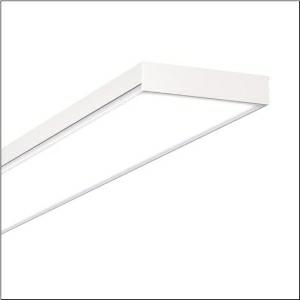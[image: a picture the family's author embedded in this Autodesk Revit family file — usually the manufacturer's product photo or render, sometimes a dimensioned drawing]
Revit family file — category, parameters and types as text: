
# Revit family: apollon_r__31_51mp26wm2441w_e1c8
name_source: partatom
category: Lighting Fixtures
units: mm (PartAtom-declared; Revit-internal decimal feet)

## family parameters
Cut with Voids When Loaded = No
Host = Face
Light Source = No
Part Type = Normal
Room Calculation Point = No
Round Connector Dimension = Use Diameter
Shared = No

## types (1)
- Apollon® 31 (1 x LED, 4600 lm, 33 W, 4000K)
    Apparent Load = 33 VA
    CIE Flux Codes = 61 87 97 97 100
    Color Rendering = 80
    Color Temperature = 4000K
    Default Elevation = 1800 mm
    Description = Apollon® 31, office luminaire, primary optical cover: micro prismatic cover, of PMMA, light emission: direct distribution, primary light characteristic: symmetric, installation type: surface-mounted, LED, rated luminous flux: 4.600lm, luminous efficacy: 139lm/W, light colour: 840, colour temperature: 4000K, control gear: ECG Multilumen, with terminal, 3-pole, mains connection: 220..240V, AC, 50/60Hz, rated input power: 33W, housing, of sheet steel, coil coated, traffic white (RAL 9016), length: 1.545mm, width: 200mm, height: 44mm, protection rating (complete): IP20, insulation class (complete): insulation class II (safety insulation), certification: CE, impact resistance: IK02, permissible operating ambient temperature: -20..+40°C, packaging unit: 1 piece
    Height = 44 mm
    Lamp = 1 x LED
    Lamp Light Flux = 4600 lm
    Lamp Power = 33 W
    Lamp count = 1
    Length = 1545 mm
    Luminous efficacy = 139 lm/W
    Manufacturer = Siteco
    ModVariant = No
    Model = 51MP26WM2441W
    Mounting Place = Ceiling
    Mounting Type = Surface mounted
    Number of Poles = 1
    OnlyDefault = Yes
    Power Factor = 1
    Product Name = Apollon® 31
    Product group = office luminaire | ceiling mounted
    ProductGroupID = 302
    Protection Class = Protection class II
    Protection Degree = IP 20
    RLX_Detail_Level = 1
    RlxData = <blob elided: 20741 chars, md5=14f4c98e>
    Socket = socket
    Standby Power = 0 W
    System Light Flux = 4600 lm
    System Power = 33 W
    Type Comments = Product without accessories
    Type Image = l_1007095.jpg
    URL = http://relux.com
    VarID = ---
    Voltage = 0 V
    Weight = 0.00 kg
    Width = 200 mm  [stored 0.656168 ft]

note: [stored X ft] marks values corroborated as IEEE doubles in the binary element streams (Revit-internal decimal feet)

## geometry (parser evidence)
native form markers: Blend x4, Sweep x9
no freeform markers — native parametric forms only
